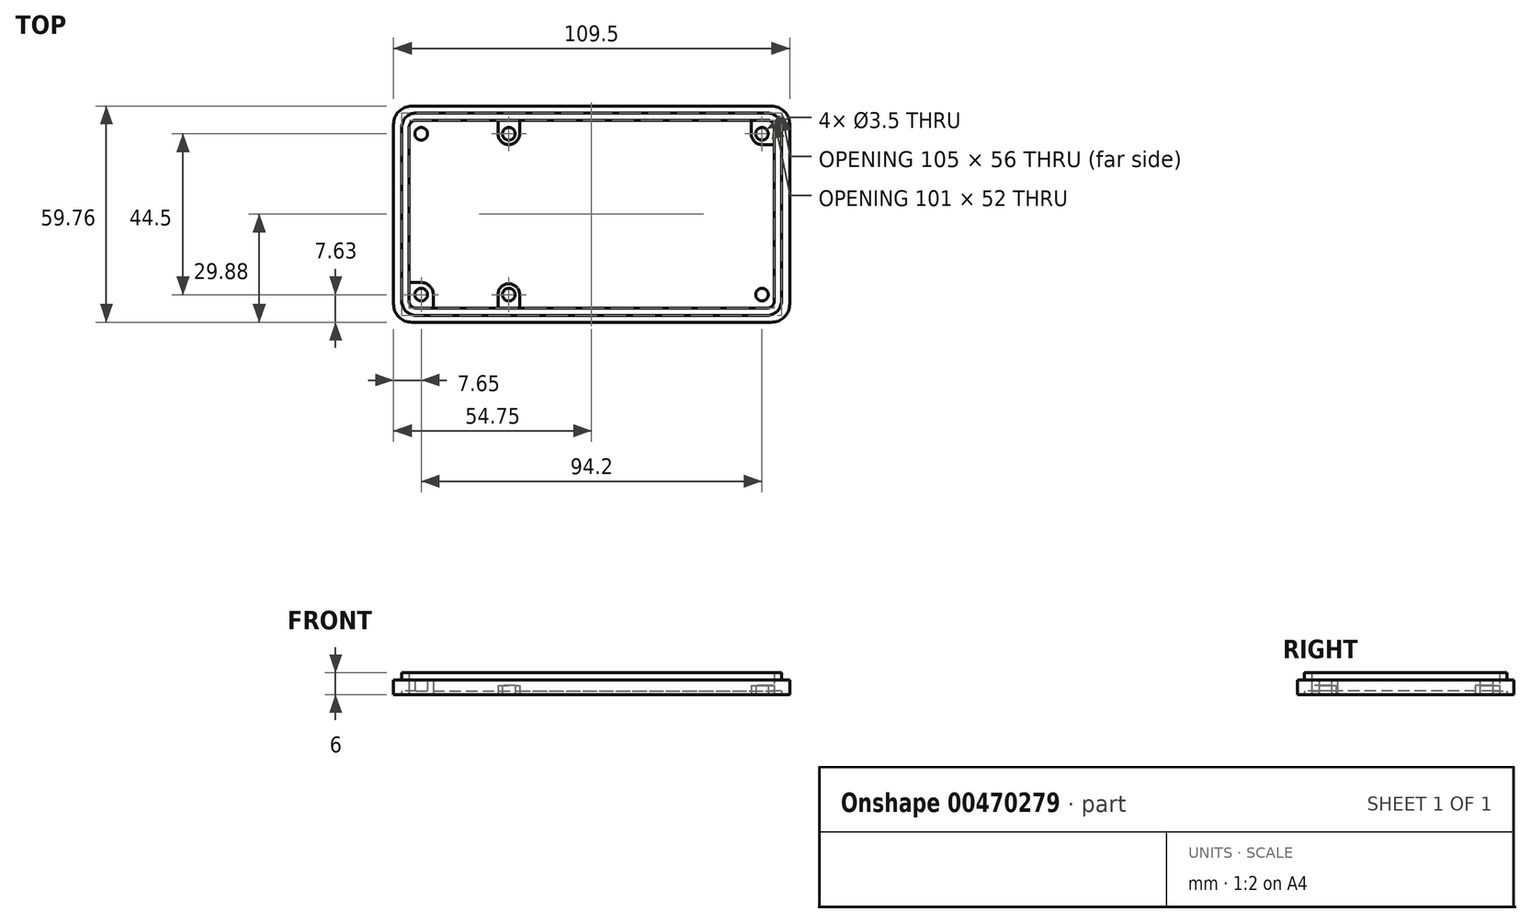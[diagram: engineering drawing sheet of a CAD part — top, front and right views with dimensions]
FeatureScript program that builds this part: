
annotation { "Feature Type Name" : "Feature", "Feature Type Description" : "" }
export const myFeature = defineFeature(function(context is Context, id is Id, definition is map)
    precondition{}
    {
        {
            var Q0;
            Q0=qCreatedBy(makeId("Top.planeOp"),FACE);
            var sketch = newSketch(context, id + "F0", { "sketchPlane" : qUnion([Q0])});
            skLineSegment(sketch, "E0.bottom", {"start": v(-48.5, 26) * mm, "end": v(48.5, 26) * mm});
            skLineSegment(sketch, "E0.top", {"start": v(-48.5, -26) * mm, "end": v(48.5, -26) * mm});
            skLineSegment(sketch, "E0.left", {"start": v(-50.5, 24) * mm, "end": v(-50.5, -24) * mm});
            skLineSegment(sketch, "E0.right", {"start": v(50.5, 24) * mm, "end": v(50.5, -24) * mm});
            skLineSegment(sketch, "E1.bottom", {"start": v(-48.5, 28) * mm, "end": v(48.5, 28) * mm});
            skLineSegment(sketch, "E1.top", {"start": v(-48.5, -28) * mm, "end": v(48.5, -28) * mm});
            skLineSegment(sketch, "E1.left", {"start": v(-52.5, 24) * mm, "end": v(-52.5, -24) * mm});
            skLineSegment(sketch, "E1.right", {"start": v(52.5, 24) * mm, "end": v(52.5, -24) * mm});
            skLineSegment(sketch, "E2", {"start": v(-77.7, 0) * mm, "end": v(77.7, 0) * mm, "construction": true});
            skLineSegment(sketch, "E3", {"start": v(0, 54.5) * mm, "end": v(0, -54.5) * mm, "construction": true});
            skCircle(sketch, "E4", {"center": v(47.1, 22.25) * mm, "radius": 1.75 * mm});
            skArc(sketch, "E5", {"start": v(44.1, 22.25) * mm, "mid": v(44.98, 20.13) * mm, "end": v(47.1, 19.25) * mm});
            skLineSegment(sketch, "E6", {"start": v(44.1, 22.25) * mm, "end": v(44.1, 26) * mm});
            skLineSegment(sketch, "E7", {"start": v(47.1, 19.25) * mm, "end": v(50.5, 19.25) * mm});
            skCircle(sketch, "E8.MirrorC", {"center": v(47.1, -22.25) * mm, "radius": 1.75 * mm});
            skLineSegment(sketch, "E9.MirrorCS", {"start": v(44.1, -22.25) * mm, "end": v(44.1, -26) * mm});
            skLineSegment(sketch, "E10.MirrorCS", {"start": v(47.1, -19.25) * mm, "end": v(50.5, -19.25) * mm});
            skArc(sketch, "E11.MirrorCS", {"start": v(44.1, -22.25) * mm, "mid": v(44.98, -20.13) * mm, "end": v(47.1, -19.25) * mm});
            skCircle(sketch, "E12.MirrorC", {"center": v(-47.1, -22.25) * mm, "radius": 1.75 * mm});
            skCircle(sketch, "E13.MirrorC", {"center": v(-47.1, 22.25) * mm, "radius": 1.75 * mm});
            skLineSegment(sketch, "E14.bottom", {"start": v(-49.75, 29.88) * mm, "end": v(49.75, 29.88) * mm});
            skLineSegment(sketch, "E14.top", {"start": v(-49.75, -29.88) * mm, "end": v(49.75, -29.88) * mm});
            skLineSegment(sketch, "E14.left", {"start": v(-54.75, 24.88) * mm, "end": v(-54.75, -24.88) * mm});
            skLineSegment(sketch, "E14.right", {"start": v(54.75, 24.88) * mm, "end": v(54.75, -24.87) * mm});
            skPoint(sketch, "E15.visualSharp", {"position": v(-54.75, 29.88) * mm});
            skArc(sketch, "E15.filletArc", {"start": v(-49.75, 29.88) * mm, "mid": v(-53.29, 28.41) * mm, "end": v(-54.75, 24.88) * mm});
            skPoint(sketch, "E16.visualSharp", {"position": v(54.75, 29.88) * mm});
            skArc(sketch, "E16.filletArc", {"start": v(54.75, 24.88) * mm, "mid": v(53.29, 28.41) * mm, "end": v(49.75, 29.88) * mm});
            skPoint(sketch, "E17.visualSharp", {"position": v(54.75, -29.88) * mm});
            skArc(sketch, "E17.filletArc", {"start": v(49.75, -29.87) * mm, "mid": v(53.29, -28.41) * mm, "end": v(54.75, -24.87) * mm});
            skPoint(sketch, "E18.visualSharp", {"position": v(-54.75, -29.88) * mm});
            skArc(sketch, "E18.filletArc", {"start": v(-54.75, -24.88) * mm, "mid": v(-53.29, -28.41) * mm, "end": v(-49.75, -29.88) * mm});
            skPoint(sketch, "E19.visualSharp", {"position": v(-52.5, 28) * mm});
            skArc(sketch, "E19.filletArc", {"start": v(-48.5, 28) * mm, "mid": v(-51.33, 26.83) * mm, "end": v(-52.5, 24) * mm});
            skPoint(sketch, "E20.visualSharp", {"position": v(52.5, 28) * mm});
            skArc(sketch, "E20.filletArc", {"start": v(52.5, 24) * mm, "mid": v(51.33, 26.83) * mm, "end": v(48.5, 28) * mm});
            skPoint(sketch, "E21.visualSharp", {"position": v(52.5, -28) * mm});
            skArc(sketch, "E21.filletArc", {"start": v(48.5, -28) * mm, "mid": v(51.33, -26.83) * mm, "end": v(52.5, -24) * mm});
            skPoint(sketch, "E22.visualSharp", {"position": v(-52.5, -28) * mm});
            skArc(sketch, "E22.filletArc", {"start": v(-52.5, -24) * mm, "mid": v(-51.33, -26.83) * mm, "end": v(-48.5, -28) * mm});
            skPoint(sketch, "E23.visualSharp", {"position": v(-50.5, -26) * mm});
            skArc(sketch, "E23.filletArc", {"start": v(-50.5, -24) * mm, "mid": v(-49.91, -25.41) * mm, "end": v(-48.5, -26) * mm});
            skPoint(sketch, "E24.visualSharp", {"position": v(-50.5, 26) * mm});
            skArc(sketch, "E24.filletArc", {"start": v(-48.5, 26) * mm, "mid": v(-49.91, 25.41) * mm, "end": v(-50.5, 24) * mm});
            skPoint(sketch, "E25.visualSharp", {"position": v(50.5, 26) * mm});
            skArc(sketch, "E25.filletArc", {"start": v(50.5, 24) * mm, "mid": v(49.91, 25.41) * mm, "end": v(48.5, 26) * mm});
            skPoint(sketch, "E26.visualSharp", {"position": v(50.5, -26) * mm});
            skArc(sketch, "E26.filletArc", {"start": v(48.5, -26) * mm, "mid": v(49.91, -25.41) * mm, "end": v(50.5, -24) * mm});
            skCircle(sketch, "E27", {"center": v(-22.9, 22.25) * mm, "radius": 1.75 * mm});
            skArc(sketch, "E28", {"start": v(-19.9, 22.25) * mm, "mid": v(-22.9, 19.25) * mm, "end": v(-25.9, 22.25) * mm});
            skLineSegment(sketch, "E29", {"start": v(-25.9, 22.25) * mm, "end": v(-25.9, 26) * mm});
            skLineSegment(sketch, "E30", {"start": v(-19.9, 22.25) * mm, "end": v(-19.9, 26) * mm});
            skLineSegment(sketch, "E31.MirrorCS", {"start": v(-25.9, -22.25) * mm, "end": v(-25.9, -26) * mm});
            skLineSegment(sketch, "E32.MirrorCS", {"start": v(-19.9, -22.25) * mm, "end": v(-19.9, -26) * mm});
            skCircle(sketch, "E33.MirrorC", {"center": v(-22.9, -22.25) * mm, "radius": 1.75 * mm});
            skArc(sketch, "E34.MirrorCS", {"start": v(-19.9, -22.25) * mm, "mid": v(-22.9, -19.25) * mm, "end": v(-25.9, -22.25) * mm});
            skArc(sketch, "E35", {"start": v(-47.1, 18.9) * mm, "mid": v(-44.73, 19.88) * mm, "end": v(-43.75, 22.25) * mm});
            skLineSegment(sketch, "E36", {"start": v(-43.75, 22.25) * mm, "end": v(-43.75, 26) * mm});
            skLineSegment(sketch, "E37", {"start": v(-47.1, 18.9) * mm, "end": v(-50.5, 18.9) * mm});
            skLineSegment(sketch, "E38.MirrorCS", {"start": v(-43.75, -22.25) * mm, "end": v(-43.75, -26) * mm});
            skLineSegment(sketch, "E39.MirrorCS", {"start": v(-47.1, -18.9) * mm, "end": v(-50.5, -18.9) * mm});
            skArc(sketch, "E40.MirrorCS", {"start": v(-47.1, -18.9) * mm, "mid": v(-44.73, -19.88) * mm, "end": v(-43.75, -22.25) * mm});
            skSolve(sketch);
        }
        {
            var Q0;
            Q0=makeQuery(id+"F0.imprint","IMPRINT",FACE,{"disambiguationData":[TD([[makeQuery(id+"F0.imprint","IMPRINT",EDGE,{"derivedFrom":sQuery(id+"F0.wireOp",EDGE,"E1.bottom")}),-1.0]])]});
            extrude(context, id + "F1", {"entities" : qUnion([Q0]), "depth" : 6 * mm});
        }
        {
            var Q0;
            Q0=makeQuery(id+"F0.imprint","IMPRINT",FACE,{"disambiguationData":[TD([[makeQuery(id+"F0.imprint","IMPRINT",EDGE,{"derivedFrom":sQuery(id+"F0.wireOp",EDGE,"E1.bottom")}),1.0]])]});
            extrude(context, id + "F2", {"entities" : qUnion([Q0]), "operationType" : NewBodyOperationType.ADD, "depth" : 4 * mm});
        }
        {
            var Q0;
            Q0=makeQuery(id+"F0.imprint","IMPRINT",FACE,{"disambiguationData":[TD([[makeQuery(id+"F0.imprint","IMPRINT",EDGE,{"derivedFrom":sQuery(id+"F0.wireOp",EDGE,"E27")}),-1.0]])]});
            var Q1;
            Q1=makeQuery(id+"F0.imprint","IMPRINT",FACE,{"disambiguationData":[TD([[makeQuery(id+"F0.imprint","IMPRINT",EDGE,{"derivedFrom":sQuery(id+"F0.wireOp",EDGE,"E4")}),-1.0]])]});
            var Q2;
            Q2=makeQuery(id+"F0.imprint","IMPRINT",FACE,{"disambiguationData":[TD([[makeQuery(id+"F0.imprint","IMPRINT",EDGE,{"derivedFrom":sQuery(id+"F0.wireOp",EDGE,"E8.MirrorC")}),1.0]])]});
            var Q3;
            {var subQ1=sQuery(id+"F0.wireOp",EDGE,"E31.MirrorCS");Q3=makeQuery(id+"F0.imprint","IMPRINT",FACE,{"disambiguationData":[TD([[makeQuery(id+"F0.imprint","IMPRINT",EDGE,{"derivedFrom":subQ1}),1.0]])]});}
            extrude(context, id + "F3", {"entities" : qUnion([Q0, Q1, Q2, Q3]), "operationType" : NewBodyOperationType.ADD, "depth" : 2.5 * mm});
        }
        {
            var Q0;
            Q0=makeQuery(id+"F0.imprint","IMPRINT",FACE,{"disambiguationData":[TD([[makeQuery(id+"F0.imprint","IMPRINT",EDGE,{"derivedFrom":sQuery(id+"F0.wireOp",EDGE,"E13.MirrorC")}),1.0]])]});
            var Q1;
            Q1=makeQuery(id+"F0.imprint","IMPRINT",FACE,{"disambiguationData":[TD([[makeQuery(id+"F0.imprint","IMPRINT",EDGE,{"derivedFrom":sQuery(id+"F0.wireOp",EDGE,"E12.MirrorC")}),-1.0]])]});
            extrude(context, id + "F4", {"entities" : qUnion([Q0, Q1]), "operationType" : NewBodyOperationType.ADD, "depth" : 4 * mm});
        }
        {
            var Q0;
            Q0=makeQuery(id+"F0.imprint","IMPRINT",FACE,{"disambiguationData":[TD([[makeQuery(id+"F0.imprint","IMPRINT",EDGE,{"derivedFrom":sQuery(id+"F0.wireOp",EDGE,"E1.bottom")}),-1.0]])]});
            extrude(context, id + "F5", {"entities" : qUnion([Q0]), "operationType" : NewBodyOperationType.REMOVE, "depth" : 1 * mm});
        }
    });
